# Revit family: IS_Alu+_BD584_BIM_NL
name_source: partatom
category: Plumbing Fixtures
units: mm (PartAtom-declared; Revit-internal decimal feet)

## family parameters
Always vertical = No
Cut with Voids When Loaded = No
OmniClass Number = 23.45.05.14.17
OmniClass Title = Showers
Part Type = Normal
Room Calculation Point = No
Round Connector Dimension = Use Diameter
Shared = No
Work Plane-Based = No

## types (3) — shared parameters
Accesoires = https://www.idealstandard.nl
Accessories = https://www.idealstandard.nl
Afmetingen = 452 x 501 x 1300 mm
AfstandsEenheid = Millimeter
AreaUnits = millimeters
AssetType = Fixed
Auteur = IdealStandard
BIMObjectName = ISI_IdealStandard_Shower mixers_Alu+_BD584
BIMobject category = Showers
BIMobject category code = showers
BIMobject main category = Sanitary
BIMobject main category code = sanitary
Beschrijvinggarantie = Herstellergarantie
BimObjectNaam = ISI_IdealStandard_Shower mixers_Alu+_BD584
Brand = Ideal Standard
Brand url = https://www.idealstandard.nl
Breedte = 451.772739
ConnectionType = Plumbing
CurrencyUnit = €
CurrentRevision = 1
Date of publishing = 01/06/2023
Debiet = 8l/min (handspray); 12l/min (showerhead)
Design country = Italy
DurationUnit = Year
Edition number = 1
Garantieonderdelen = 5
Garantieunits = Jaren
GemaaktOp = 01/06/2023
Help = https://www.idealstandard.nl
Hoogte = 1300,6611774065
Hulp = https://www.idealstandard.nl
IFC Classification = Sanitary Terminal
IfcExportAs = IfcValveType
IfcExportType = FAUCET
Installatieinstructies = https://www.idealstandard.nl
Installation instructions = https://www.idealstandard.nl
InstallationInstructions = https://www.idealstandard.nl
Lengte = 501 mm
LinearUnits = millimeters
MaintenanceInformation = https://www.idealstandard.nl
Manufacturer = Ideal Standard
Manufacturer name = Ideal Standard
ManufacturerURL = https://www.idealstandard.nl
Materiaal = Messing
Material = Brass
Material main = Brass
Merk = Ideal Standard
NBS Reference Code = 45-35-70/315
NBS Reference Description = Shower mixers
Name = Shower mixers_Alu+_BD584_IdealStandard
NettWeight = 7,12
NominalDepth = 501 mm
NominalHeight = 1301 mm
NominalLength = 501 mm
NominalWidth = 452 mm
OmniClass Code = 23-31 11 00
OmniClass Description = Faucets
OppervlakteEenheid = Millimeter
Product Guid = 97f92a8f-6fa4-4572-872b-15b2f79888b5
Product SKU = BD584
Product certification = https://www.idealstandard.nl
Product data url = https://bimobject.com
Product family = Alu+
Product group = Alu+
Product name = CERAFLOW ALU+ SHR SYS SL 2F 260MM 2S RO
Product url = https://www.idealstandard.nl
ProductInformation = https://www.idealstandard.nl
ProductSoort = Sanitary
Productinformatie = https://www.idealstandard.nl
QR code = http://bimobject.com
Revisie = 1
Shape = Cylindrical
Size = 452 x 501 x 1300 mm
Space = Internal
SpareParts = https://www.idealstandard.nl
Technical description = https://www.idealstandard.nl
Telefoonnummer = 077 355 08 08
TestPressure = 10 bar
Typeconnectie = Installation
UNSPSC Code = 30181700
URL = https://www.idealstandard.nl
Uniclass 1.4 Code = L725111
Uniclass 1.4 Description = Mixer taps
Uniclass 2.0 Code = Pr_40_30_96_81
Uniclass 2.0 Description = Shower Thermostatic Water Supply Sets
Uniclass 2015 Code = Pr_40_20_87_78
Uniclass 2015 Name = Shower manual water supply sets
Uniclass2015Beschrijving = Pr_40_20_87_78
Uniclass2015Code = Pr_40_20_87_78
Uniclass2015Referentie = Pr_40_20_87_78
Uniclass2015Title = Shower manual water supply sets
Uniclass2015Version = v1.20
Urlproducent = https://www.idealstandard.nl
ValutaEenheid = €
Version = 1
VolumeUnits = Litres
Volumeunits = Liters
Vorm = zylindrisch
WRASURL = https://www.wrasapprovals.co.uk
WarrantyDescription = Manufacturers Warranty
WarrantyDurationParts = 5
WarrantyDurationUnit = Year
WarrantyGuarantorParts = https://www.idealstandard.nl
Weight Net (Kg) = 7.12
Youtube clip = https://www.youtube.com
zero-valued in all types: BrutoGewicht, Default Elevation, Diepte, Nettogewicht, Vervangingskosten

## per-type parameters (varying)
| type | Afwerking | Artikelnummer | Artikelomschrijving | Artikelreferentie | BarCode | Barcode | Color | Description | Features | Finish | GTIN code | Kleur | MainColor | Model | ModelNumber |
| BD584RO - CERAFLOW ALU+ SHR SYS SL 2F 260MM 2S RO | Roos | BD584RO | CERAFLOW ALU+ SHR SYS SL 2F 260MM 2S RO | CERAFLOW ALU+ SHR SYS SL 2F 260MM 2S RO | 3800861117414 | 3800861117414 | Rose | Ceraflow Alu+ Douchesysteem 260MM 2 Functie Douchekop 12l/min, 100mm 2 Functie Idealrain Alu+ Handdouche 8l/min, omstelling geïntegreerd in de handgreep, water- en energiebesparing, easyfix, inclusief gladde, gemakkelijk te reinigen en duurzame idealflex gaatjes, standaard s-connectors, heetwaterbegrenzer, koele behuizingstechnologie, 2-weg omstelling geïntegreerd in de behuizing, rosé. | Ceraflow Alu+ Douchesysteem 260MM 2 Functie Douchekop 12l/min, 100mm 2 Functie Idealrain Alu+ Handdouche 8l/min, omstelling geïntegreerd in de handgreep, water- en energiebesparing, easyfix, inclusief gladde, gemakkelijk te reinigen en duurzame idealflex gaatjes, standaard s-connectors, heetwaterbegrenzer, koele behuizingstechnologie, 2-weg omstelling geïntegreerd in de behuizing, rosé. | Rose | 3800861117414 | Roos | Rose | BD584RO | BD584RO |
| BD584SI - CERAFLOW ALU+ SHR SYS SL 2F 260MM 2S SI | Zilver | BD584SI | CERAFLOW ALU+ SHR SYS SL 2F 260MM 2S SI | CERAFLOW ALU+ SHR SYS SL 2F 260MM 2S SI | 3800861117292 | 3800861117292 | Silver | Ceraflow Alu+ Douchesysteem 260MM 2 Functie Douchekop 12l/min, 100mm 2 Functie Idealrain Alu+ Handdouche 8l/min, omstelling geïntegreerd in de handgreep, water- en energiebesparing, easyfix, inclusief gladde, gemakkelijk te reinigen en duurzame idealflex gaatjes, standaard s-connectors, heetwaterbegrenzer, koele behuizingstechnologie, 2-weg omstelling geïntegreerd in de behuizing, zilver. | Ceraflow Alu+ Douchesysteem 260MM 2 Functie Douchekop 12l/min, 100mm 2 Functie Idealrain Alu+ Handdouche 8l/min, omstelling geïntegreerd in de handgreep, water- en energiebesparing, easyfix, inclusief gladde, gemakkelijk te reinigen en duurzame idealflex gaatjes, standaard s-connectors, heetwaterbegrenzer, koele behuizingstechnologie, 2-weg omstelling geïntegreerd in de behuizing, zilver. | Silver | 3800861117292 | Zilver | Silver | BD584SI | BD584SI |
| BD584XG - CERAFLOW ALU+ SHR SYS SL 2F 260MM 2S XG | Zijde Zwart | BD584XG | CERAFLOW ALU+ SHR SYS SL 2F 260MM 2S XG | CERAFLOW ALU+ SHR SYS SL 2F 260MM 2S XG | 3800861117179 | 3800861117179 | Silk Black | Ceraflow Alu+ Douchesysteem 260MM 2 Functie Douchekop 12l/min, 100mm 2 Functie Idealrain Alu+ Handdouche 8l/min, omstelling geïntegreerd in de handgreep, water- en energiebesparing, easyfix, inclusief gladde, gemakkelijk te reinigen en duurzame idealflex gaatjes, standaard s-connectors, heetwaterbegrenzer, koele behuizingstechnologie, 2-weg omstelling geïntegreerd in de behuizing, zijdezwart. | Ceraflow Alu+ Douchesysteem 260MM 2 Functie Douchekop 12l/min, 100mm 2 Functie Idealrain Alu+ Handdouche 8l/min, omstelling geïntegreerd in de handgreep, water- en energiebesparing, easyfix, inclusief gladde, gemakkelijk te reinigen en duurzame idealflex gaatjes, standaard s-connectors, heetwaterbegrenzer, koele behuizingstechnologie, 2-weg omstelling geïntegreerd in de behuizing, zijdezwart. | Silk Black | 3800861117179 | Zijde Zwart | Silk Black | BD584XG | BD584XG |

note: column(s) folded — value = type name in every type: Eigenschappen, ModelReference, Referentie

## geometry (parser evidence)
native form markers: Blend x2, Sweep x4
no freeform markers — native parametric forms only
